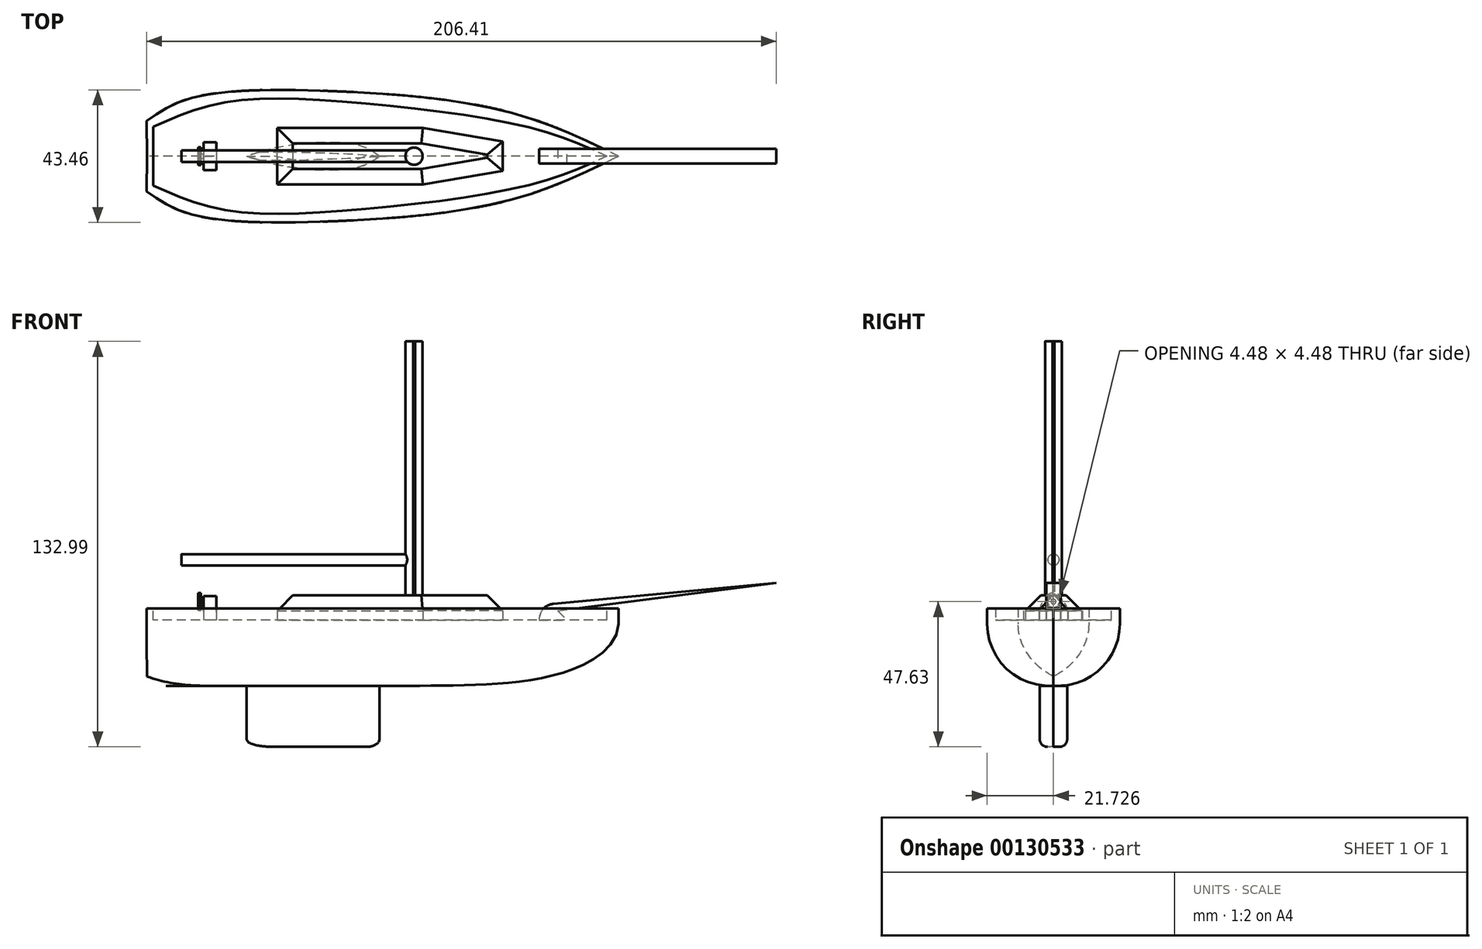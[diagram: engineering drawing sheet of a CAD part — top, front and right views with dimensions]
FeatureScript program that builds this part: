
annotation { "Feature Type Name" : "Feature", "Feature Type Description" : "" }
export const myFeature = defineFeature(function(context is Context, id is Id, definition is map)
    precondition{}
    {
        {
            var Q0;
            Q0=qCreatedBy(makeId("Top.planeOp"),FACE);
            var sketch = newSketch(context, id + "F0", { "sketchPlane" : qUnion([Q0])});
            skLineSegment(sketch, "E0", {"start": v(-76.13, 0) * mm, "end": v(78.37, 0) * mm});
            skFitSpline(sketch, "E1", {"points": [v(78.37, 0) * mm, v(42.4, 14.48) * mm, v(-15.41, 21.34) * mm, v(-61.78, 19.05) * mm, v(-76.34, 11.57) * mm], "startDerivative": vector(-132.35, 64.75) * mm, "endDerivative": vector(-74.5, -52.24) * mm});
            skLineSegment(sketch, "E2", {"start": v(-76.34, 11.57) * mm, "end": v(-76.13, 0) * mm});
            skFitSpline(sketch, "E3.MirrorCS", {"points": [v(78.37, 0) * mm, v(42.4, -14.48) * mm, v(-15.41, -21.34) * mm, v(-61.78, -19.05) * mm, v(-76.34, -11.57) * mm], "startDerivative": vector(-132.35, -64.75) * mm, "endDerivative": vector(-74.5, 52.24) * mm});
            skLineSegment(sketch, "E4.MirrorCS", {"start": v(-76.34, -11.57) * mm, "end": v(-76.13, 0) * mm});
            skSolve(sketch);
        }
        {
            var Q0;
            Q0=makeQuery(id+"F0.imprint","IMPRINT",FACE,{"disambiguationData":[TD([[makeQuery(id+"F0.imprint","IMPRINT",EDGE,{"derivedFrom":sQuery(id+"F0.wireOp",EDGE,"E0")}),1.0]])]});
            var Q1;
            Q1=makeQuery(id+"F0.imprint","IMPRINT",FACE,{"disambiguationData":[TD([[makeQuery(id+"F0.imprint","IMPRINT",EDGE,{"derivedFrom":sQuery(id+"F0.wireOp",EDGE,"E0")}),-1.0]])]});
            extrude(context, id + "F1", {"entities" : qUnion([Q0, Q1]), "depth" : 25.4 * mm});
        }
        {
            var Q0;
            Q0=makeQuery(id+"F1.opExtrude","CAP_EDGE",EDGE,{"disambiguationData":[OSD([sQuery(id+"F0.wireOp",EDGE,"E3.MirrorCS")])],"isStart":true});
            var Q1;
            Q1=makeQuery(id+"F1.opExtrude","CAP_EDGE",EDGE,{"disambiguationData":[OSD([sQuery(id+"F0.wireOp",EDGE,"E1")])],"isStart":true});
            var Q2;
            Q2=makeQuery(id+"F1.opExtrude","CAP_EDGE",EDGE,{"disambiguationData":[OSD([sQuery(id+"F0.wireOp",EDGE,"E4.MirrorCS")])],"isStart":true});
            var Q3;
            Q3=makeQuery(id+"F1.opExtrude","CAP_EDGE",EDGE,{"disambiguationData":[OSD([sQuery(id+"F0.wireOp",EDGE,"E2")])],"isStart":true});
            fillet(context, id + "F2", {"entities" : qUnion([Q0, Q1, Q2, Q3]), "radius" : 20.32 * mm, "tangentPropagation" : true, "allowEdgeOverflow" : false});
        }
        {
            var Q0;
            Q0=makeQuery(id+"F1.opExtrude","CAP_FACE",FACE,{"disambiguationData":[OSD([sQuery(id+"F0.wireOp",EDGE,"E1"),sQuery(id+"F0.wireOp",EDGE,"E2"),sQuery(id+"F0.wireOp",EDGE,"E3.MirrorCS"),sQuery(id+"F0.wireOp",EDGE,"E4.MirrorCS")])],"isStart":false});
            var sketch = newSketch(context, id + "F3", { "sketchPlane" : qUnion([Q0])});
            skLineSegment(sketch, "E5", {"start": v(-76.13, 0) * mm, "end": v(78.37, 0) * mm});
            skFitSpline(sketch, "E6", {"points": [v(74.55, 0) * mm, v(49.26, -9.4) * mm, v(-9.25, -17.68) * mm, v(-51, -17.59) * mm, v(-74.11, -9.66) * mm], "startDerivative": vector(-102.53, -46.86) * mm, "endDerivative": vector(-106.23, 46.73) * mm});
            skLineSegment(sketch, "E7", {"start": v(-74.11, -9.66) * mm, "end": v(-74.11, 0) * mm});
            skLineSegment(sketch, "E8.MirrorCS", {"start": v(-74.11, 9.66) * mm, "end": v(-74.11, 0) * mm});
            skFitSpline(sketch, "E9.MirrorCS", {"points": [v(74.55, 0) * mm, v(49.26, 9.4) * mm, v(-9.25, 17.68) * mm, v(-51, 17.59) * mm, v(-74.11, 9.66) * mm], "startDerivative": vector(-102.53, 46.86) * mm, "endDerivative": vector(-106.23, -46.73) * mm});
            skSolve(sketch);
        }
        {
            var Q0;
            Q0 = qSketchRegion(id + "F3", true);
            extrude(context, id + "F4", {"entities" : qUnion([Q0]), "operationType" : NewBodyOperationType.REMOVE, "oppositeDirection" : true, "depth" : 3.82 * mm});
        }
        {
            var Q0;
            Q0=makeQuery(id+"F4.boolean.opBoolean","COPY",FACE,{"derivedFrom":makeQuery(id+"F4.opExtrude","CAP_FACE",FACE,{"disambiguationData":[OSD([sQuery(id+"F3.wireOp",EDGE,"E6"),sQuery(id+"F3.wireOp",EDGE,"E7"),sQuery(id+"F3.wireOp",EDGE,"E8.MirrorCS"),sQuery(id+"F3.wireOp",EDGE,"E9.MirrorCS")])],"isStart":false})});
            var sketch = newSketch(context, id + "F5", { "sketchPlane" : qUnion([Q0])});
            skLineSegment(sketch, "E10", {"start": v(-74.11, 0) * mm, "end": v(74.55, 0) * mm});
            skLineSegment(sketch, "E11.bottom", {"start": v(-33.52, 9.26) * mm, "end": v(14.21, 9.26) * mm});
            skLineSegment(sketch, "E11.top", {"start": v(-33.52, -9.26) * mm, "end": v(14.21, -9.26) * mm});
            skLineSegment(sketch, "E11.left", {"start": v(-33.52, 9.26) * mm, "end": v(-33.52, -9.26) * mm});
            skLineSegment(sketch, "E11.right", {"start": v(14.21, 9.26) * mm, "end": v(14.21, -9.26) * mm});
            skPoint(sketch, "E11.middle", {"position": v(-9.66, 0) * mm});
            skLineSegment(sketch, "E12", {"start": v(14.21, -9.26) * mm, "end": v(40.42, -4.78) * mm});
            skLineSegment(sketch, "E13", {"start": v(40.42, -4.78) * mm, "end": v(40.42, 0) * mm});
            skLineSegment(sketch, "E14.MirrorCS", {"start": v(14.21, 9.26) * mm, "end": v(40.42, 4.78) * mm});
            skLineSegment(sketch, "E15.MirrorCS", {"start": v(40.42, 4.78) * mm, "end": v(40.42, 0) * mm});
            skLineSegment(sketch, "E16.bottom", {"start": v(-53.41, 4.58) * mm, "end": v(-57.62, 4.58) * mm});
            skLineSegment(sketch, "E16.top", {"start": v(-53.41, -4.58) * mm, "end": v(-57.62, -4.58) * mm});
            skLineSegment(sketch, "E16.left", {"start": v(-53.41, 4.58) * mm, "end": v(-53.41, -4.58) * mm});
            skLineSegment(sketch, "E16.right", {"start": v(-57.62, 4.58) * mm, "end": v(-57.62, -4.58) * mm});
            skPoint(sketch, "E16.middle", {"position": v(-55.52, 0) * mm});
            skSolve(sketch);
        }
        {
            var Q0;
            {var subQ5=sQuery(id+"F5.wireOp",EDGE,"E11.bottom");Q0=makeQuery(id+"F5.imprint","IMPRINT",FACE,{"disambiguationData":[TD([[makeQuery(id+"F5.imprint","IMPRINT",EDGE,{"derivedFrom":subQ5}),-1.0]])]});}
            var Q1;
            {var subQ5=sQuery(id+"F5.wireOp",EDGE,"E11.top");Q1=makeQuery(id+"F5.imprint","IMPRINT",FACE,{"disambiguationData":[TD([[makeQuery(id+"F5.imprint","IMPRINT",EDGE,{"derivedFrom":subQ5}),1.0]])]});}
            var Q2;
            {var subQ4=sQuery(id+"F5.wireOp",EDGE,"E14.MirrorCS");Q2=makeQuery(id+"F5.imprint","IMPRINT",FACE,{"disambiguationData":[TD([[makeQuery(id+"F5.imprint","IMPRINT",EDGE,{"derivedFrom":subQ4}),-1.0]])]});}
            var Q3;
            {var subQ4=sQuery(id+"F5.wireOp",EDGE,"E12");Q3=makeQuery(id+"F5.imprint","IMPRINT",FACE,{"disambiguationData":[TD([[makeQuery(id+"F5.imprint","IMPRINT",EDGE,{"derivedFrom":subQ4}),1.0]])]});}
            extrude(context, id + "F6", {"entities" : qUnion([Q0, Q1, Q2, Q3]), "operationType" : NewBodyOperationType.ADD, "depth" : 8.06 * mm});
        }
        {
            var Q0;
            {var subQ5=sQuery(id+"F5.wireOp",EDGE,"E16.bottom");Q0=makeQuery(id+"F5.imprint","IMPRINT",FACE,{"disambiguationData":[TD([[makeQuery(id+"F5.imprint","IMPRINT",EDGE,{"derivedFrom":subQ5}),1.0]])]});}
            var Q1;
            {var subQ5=sQuery(id+"F5.wireOp",EDGE,"E16.top");Q1=makeQuery(id+"F5.imprint","IMPRINT",FACE,{"disambiguationData":[TD([[makeQuery(id+"F5.imprint","IMPRINT",EDGE,{"derivedFrom":subQ5}),-1.0]])]});}
            extrude(context, id + "F7", {"entities" : qUnion([Q0, Q1]), "operationType" : NewBodyOperationType.ADD, "depth" : 7.85 * mm});
        }
        {
            var Q0;
            Q0=makeQuery(id+"F7.opExtrude","CAP_EDGE",EDGE,{"disambiguationData":[OSD([sQuery(id+"F5.wireOp",EDGE,"E16.bottom")])],"isStart":false});
            var Q1;
            Q1=makeQuery(id+"F7.opExtrude","CAP_EDGE",EDGE,{"disambiguationData":[OSD([sQuery(id+"F5.wireOp",EDGE,"E16.top")])],"isStart":false});
            fillet(context, id + "F8", {"entities" : qUnion([Q0, Q1]), "radius" : 5.08 * mm, "tangentPropagation" : true, "allowEdgeOverflow" : false});
        }
        {
            var Q0;
            Q0=makeQuery(id+"F6.opExtrude","CAP_EDGE",EDGE,{"disambiguationData":[OSD([sQuery(id+"F5.wireOp",EDGE,"E11.bottom")])],"isStart":false});
            var Q1;
            Q1=makeQuery(id+"F6.opExtrude","CAP_EDGE",EDGE,{"disambiguationData":[OSD([sQuery(id+"F5.wireOp",EDGE,"E11.left")])],"isStart":false});
            var Q2;
            Q2=makeQuery(id+"F6.opExtrude","CAP_EDGE",EDGE,{"disambiguationData":[OSD([sQuery(id+"F5.wireOp",EDGE,"E11.top")])],"isStart":false});
            var Q3;
            Q3=makeQuery(id+"F6.opExtrude","CAP_EDGE",EDGE,{"disambiguationData":[OSD([sQuery(id+"F5.wireOp",EDGE,"E12")])],"isStart":false});
            var Q4;
            Q4=makeQuery(id+"F6.opExtrude","CAP_EDGE",EDGE,{"disambiguationData":[OSD([sQuery(id+"F5.wireOp",EDGE,"E14.MirrorCS")])],"isStart":false});
            var Q5;
            Q5=makeQuery(id+"F6.opExtrude","CAP_EDGE",EDGE,{"disambiguationData":[OSD([sQuery(id+"F5.wireOp",EDGE,"E13"),sQuery(id+"F5.wireOp",EDGE,"E15.MirrorCS")])],"isStart":false});
            chamfer(context, id + "F9", {"entities" : qUnion([Q0, Q1, Q2, Q3, Q4, Q5]), "width" : 5.08 * mm, "tangentPropagation" : true});
        }
        {
            var Q0;
            Q0=makeQuery(id+"F7.opExtrude","SWEPT_FACE",FACE,{"disambiguationData":[OSD([sQuery(id+"F5.wireOp",EDGE,"E16.right")])]});
            var sketch = newSketch(context, id + "F10", { "sketchPlane" : qUnion([Q0])});
            skLineSegment(sketch, "E17", {"start": v(0, 29.4) * mm, "end": v(0, 21.58) * mm});
            skCircle(sketch, "E18", {"center": v(0, 27.62) * mm, "radius": 0.8 * mm});
            skSolve(sketch);
        }
        {
            var Q0;
            Q0 = qSketchRegion(id + "F10", true);
            extrude(context, id + "F11", {"entities" : qUnion([Q0]), "operationType" : NewBodyOperationType.ADD, "depth" : 0.96 * mm});
        }
        {
            var Q0;
            Q0=makeQuery(id+"F11.opExtrude","CAP_FACE",FACE,{"disambiguationData":[OSD([sQuery(id+"F10.wireOp",EDGE,"E18")])],"isStart":false});
            var sketch = newSketch(context, id + "F12", { "sketchPlane" : qUnion([Q0])});
            skPoint(sketch, "E19", {"position": v(0, 27.62) * mm});
            skCircle(sketch, "E20", {"center": v(0, 27.62) * mm, "radius": 2.88 * mm});
            skLineSegment(sketch, "E21", {"start": v(0, 27.62) * mm, "end": v(-2.88, 27.62) * mm});
            skLineSegment(sketch, "E22", {"start": v(-2.88, 27.62) * mm, "end": v(2.88, 27.62) * mm});
            skLineSegment(sketch, "E23", {"start": v(2.88, 27.62) * mm, "end": v(0, 27.62) * mm});
            skLineSegment(sketch, "E24", {"start": v(0, 27.62) * mm, "end": v(0, 24.75) * mm});
            skLineSegment(sketch, "E25", {"start": v(0, 24.75) * mm, "end": v(0, 30.5) * mm});
            skLineSegment(sketch, "E26", {"start": v(0, 30.5) * mm, "end": v(-2.88, 30.5) * mm});
            skLineSegment(sketch, "E27", {"start": v(-2.88, 27.62) * mm, "end": v(-2.88, 30.5) * mm});
            skLineSegment(sketch, "E28", {"start": v(0, 30.5) * mm, "end": v(2.88, 30.5) * mm});
            skLineSegment(sketch, "E29", {"start": v(2.88, 27.62) * mm, "end": v(2.88, 30.5) * mm});
            skLineSegment(sketch, "E30", {"start": v(2.88, 27.62) * mm, "end": v(2.88, 24.75) * mm});
            skLineSegment(sketch, "E31", {"start": v(0, 24.75) * mm, "end": v(2.88, 24.75) * mm});
            skLineSegment(sketch, "E32", {"start": v(0, 24.75) * mm, "end": v(-2.88, 24.75) * mm});
            skLineSegment(sketch, "E33", {"start": v(-2.88, 27.62) * mm, "end": v(-2.88, 24.75) * mm});
            skLineSegment(sketch, "E34", {"start": v(0, 27.62) * mm, "end": v(2.88, 30.5) * mm});
            skLineSegment(sketch, "E35", {"start": v(0, 27.62) * mm, "end": v(2.88, 24.75) * mm});
            skLineSegment(sketch, "E36", {"start": v(0, 27.62) * mm, "end": v(-2.88, 24.75) * mm});
            skLineSegment(sketch, "E37", {"start": v(0, 27.62) * mm, "end": v(-2.88, 30.5) * mm});
            skCircle(sketch, "E38", {"center": v(0, 27.62) * mm, "radius": 1.88 * mm});
            skCircle(sketch, "E39", {"center": v(-1.33, 28.96) * mm, "radius": 0.36 * mm});
            skCircle(sketch, "E40", {"center": v(0, 29.5) * mm, "radius": 0.36 * mm});
            skCircle(sketch, "E41", {"center": v(1.33, 28.96) * mm, "radius": 0.35 * mm});
            skCircle(sketch, "E42", {"center": v(1.88, 27.62) * mm, "radius": 0.36 * mm});
            skCircle(sketch, "E43", {"center": v(1.33, 26.3) * mm, "radius": 0.36 * mm});
            skCircle(sketch, "E44", {"center": v(0, 25.74) * mm, "radius": 0.36 * mm});
            skCircle(sketch, "E45", {"center": v(-1.33, 26.3) * mm, "radius": 0.36 * mm});
            skCircle(sketch, "E46", {"center": v(-1.88, 27.62) * mm, "radius": 0.35 * mm});
            skSolve(sketch);
        }
        {
            var Q0;
            {var subQ5=sQuery(id+"F12.wireOp",EDGE,"E34");var subQ6=sQuery(id+"F12.wireOp",EDGE,"E20");var subQ7=makeQuery(id+"F12.imprint","INTERSECT",VERTEX,{"derivedFrom":[subQ6,subQ5]});Q0=makeQuery(id+"F12.imprint","IMPRINT",FACE,{"disambiguationData":[TD([[makeQuery(id+"F12.imprint","IMPRINT",EDGE,{"disambiguationData":[TD([[subQ7,1.0]])],"derivedFrom":subQ5}),-1.0]])]});}
            var Q1;
            {var subQ5=sQuery(id+"F12.wireOp",EDGE,"E34");var subQ6=sQuery(id+"F12.wireOp",EDGE,"E20");var subQ7=makeQuery(id+"F12.imprint","INTERSECT",VERTEX,{"derivedFrom":[subQ6,subQ5]});Q1=makeQuery(id+"F12.imprint","IMPRINT",FACE,{"disambiguationData":[TD([[makeQuery(id+"F12.imprint","IMPRINT",EDGE,{"disambiguationData":[TD([[subQ7,1.0]])],"derivedFrom":subQ5}),1.0]])]});}
            var Q2;
            {var subQ5=sQuery(id+"F12.wireOp",EDGE,"E37");var subQ6=sQuery(id+"F12.wireOp",EDGE,"E20");var subQ7=makeQuery(id+"F12.imprint","INTERSECT",VERTEX,{"derivedFrom":[subQ6,subQ5]});Q2=makeQuery(id+"F12.imprint","IMPRINT",FACE,{"disambiguationData":[TD([[makeQuery(id+"F12.imprint","IMPRINT",EDGE,{"disambiguationData":[TD([[subQ7,1.0]])],"derivedFrom":subQ5}),-1.0]])]});}
            var Q3;
            {var subQ5=sQuery(id+"F12.wireOp",EDGE,"E37");var subQ6=sQuery(id+"F12.wireOp",EDGE,"E20");var subQ7=makeQuery(id+"F12.imprint","INTERSECT",VERTEX,{"derivedFrom":[subQ6,subQ5]});Q3=makeQuery(id+"F12.imprint","IMPRINT",FACE,{"disambiguationData":[TD([[makeQuery(id+"F12.imprint","IMPRINT",EDGE,{"disambiguationData":[TD([[subQ7,1.0]])],"derivedFrom":subQ5}),1.0]])]});}
            var Q4;
            {var subQ5=sQuery(id+"F12.wireOp",EDGE,"E36");var subQ6=sQuery(id+"F12.wireOp",EDGE,"E20");var subQ7=makeQuery(id+"F12.imprint","INTERSECT",VERTEX,{"derivedFrom":[subQ6,subQ5]});Q4=makeQuery(id+"F12.imprint","IMPRINT",FACE,{"disambiguationData":[TD([[makeQuery(id+"F12.imprint","IMPRINT",EDGE,{"disambiguationData":[TD([[subQ7,1.0]])],"derivedFrom":subQ5}),-1.0]])]});}
            var Q5;
            {var subQ7=sQuery(id+"F12.wireOp",EDGE,"E36");var subQ8=sQuery(id+"F12.wireOp",EDGE,"E20");var subQ9=makeQuery(id+"F12.imprint","INTERSECT",VERTEX,{"derivedFrom":[subQ8,subQ7]});Q5=makeQuery(id+"F12.imprint","IMPRINT",FACE,{"disambiguationData":[TD([[makeQuery(id+"F12.imprint","IMPRINT",EDGE,{"disambiguationData":[TD([[subQ9,1.0]])],"derivedFrom":subQ7}),1.0]])]});}
            var Q6;
            {var subQ5=sQuery(id+"F12.wireOp",EDGE,"E35");var subQ6=sQuery(id+"F12.wireOp",EDGE,"E20");var subQ7=makeQuery(id+"F12.imprint","INTERSECT",VERTEX,{"derivedFrom":[subQ6,subQ5]});Q6=makeQuery(id+"F12.imprint","IMPRINT",FACE,{"disambiguationData":[TD([[makeQuery(id+"F12.imprint","IMPRINT",EDGE,{"disambiguationData":[TD([[subQ7,1.0]])],"derivedFrom":subQ5}),-1.0]])]});}
            var Q7;
            {var subQ5=sQuery(id+"F12.wireOp",EDGE,"E35");var subQ6=sQuery(id+"F12.wireOp",EDGE,"E20");var subQ7=makeQuery(id+"F12.imprint","INTERSECT",VERTEX,{"derivedFrom":[subQ6,subQ5]});Q7=makeQuery(id+"F12.imprint","IMPRINT",FACE,{"disambiguationData":[TD([[makeQuery(id+"F12.imprint","IMPRINT",EDGE,{"disambiguationData":[TD([[subQ7,1.0]])],"derivedFrom":subQ5}),1.0]])]});}
            var Q8;
            {var subQ5=sQuery(id+"F12.wireOp",EDGE,"E46");var subQ7=sQuery(id+"F12.wireOp",EDGE,"E22");var subQ11=makeQuery(id+"F12.imprint","INTERSECT",VERTEX,{"disambiguationData":[OD(1.0)],"derivedFrom":[subQ7,subQ5]});Q8=makeQuery(id+"F12.imprint","IMPRINT",FACE,{"disambiguationData":[TD([[makeQuery(id+"F12.imprint","IMPRINT",EDGE,{"disambiguationData":[TD([[subQ11,-1.0]])],"derivedFrom":subQ7}),1.0]])]});}
            var Q9;
            {var subQ0=sQuery(id+"F12.wireOp",EDGE,"E40");var subQ1=sQuery(id+"F12.wireOp",EDGE,"E25");var subQ2=makeQuery(id+"F12.imprint","INTERSECT",VERTEX,{"disambiguationData":[OD(0.0)],"derivedFrom":[subQ1,subQ0]});Q9=makeQuery(id+"F12.imprint","IMPRINT",FACE,{"disambiguationData":[TD([[makeQuery(id+"F12.imprint","IMPRINT",EDGE,{"disambiguationData":[TD([[subQ2,1.0]])],"derivedFrom":subQ1}),-1.0]])]});}
            var Q10;
            {var subQ0=sQuery(id+"F12.wireOp",EDGE,"E42");var subQ1=sQuery(id+"F12.wireOp",EDGE,"E23");var subQ2=makeQuery(id+"F12.imprint","INTERSECT",VERTEX,{"disambiguationData":[OD(1.0)],"derivedFrom":[subQ1,subQ0]});Q10=makeQuery(id+"F12.imprint","IMPRINT",FACE,{"disambiguationData":[TD([[makeQuery(id+"F12.imprint","IMPRINT",EDGE,{"disambiguationData":[TD([[subQ2,-1.0]])],"derivedFrom":subQ1}),1.0]])]});}
            var Q11;
            {var subQ3=sQuery(id+"F12.wireOp",EDGE,"E44");var subQ5=sQuery(id+"F12.wireOp",EDGE,"E25");var subQ6=makeQuery(id+"F12.imprint","INTERSECT",VERTEX,{"disambiguationData":[OD(1.0)],"derivedFrom":[subQ5,subQ3]});Q11=makeQuery(id+"F12.imprint","IMPRINT",FACE,{"disambiguationData":[TD([[makeQuery(id+"F12.imprint","IMPRINT",EDGE,{"disambiguationData":[TD([[subQ6,-1.0]])],"derivedFrom":subQ5}),1.0]])]});}
            var Q12;
            {var subQ1=sQuery(id+"F12.wireOp",EDGE,"E25");var subQ3=makeQuery(id+"F11.opExtrude","CAP_EDGE",EDGE,{"disambiguationData":[OSD([sQuery(id+"F10.wireOp",EDGE,"E18")])],"isStart":false});var subQ4=makeQuery(id+"F12.imprint","INTERSECT",VERTEX,{"disambiguationData":[OD(1.0)],"derivedFrom":[subQ3,subQ1]});Q12=makeQuery(id+"F12.imprint","IMPRINT",FACE,{"disambiguationData":[TD([[makeQuery(id+"F12.imprint","IMPRINT",EDGE,{"disambiguationData":[TD([[subQ4,1.0]])],"derivedFrom":subQ3}),1.0]])]});}
            var Q13;
            {var subQ1=sQuery(id+"F12.wireOp",EDGE,"E22");var subQ3=makeQuery(id+"F11.opExtrude","CAP_EDGE",EDGE,{"disambiguationData":[OSD([sQuery(id+"F10.wireOp",EDGE,"E18")])],"isStart":false});var subQ4=makeQuery(id+"F12.imprint","INTERSECT",VERTEX,{"derivedFrom":[subQ3,subQ1]});Q13=makeQuery(id+"F12.imprint","IMPRINT",FACE,{"disambiguationData":[TD([[makeQuery(id+"F12.imprint","IMPRINT",EDGE,{"disambiguationData":[TD([[subQ4,1.0]])],"derivedFrom":subQ3}),1.0]])]});}
            var Q14;
            {var subQ1=sQuery(id+"F12.wireOp",EDGE,"E22");var subQ3=makeQuery(id+"F11.opExtrude","CAP_EDGE",EDGE,{"disambiguationData":[OSD([sQuery(id+"F10.wireOp",EDGE,"E18")])],"isStart":false});var subQ4=makeQuery(id+"F12.imprint","INTERSECT",VERTEX,{"derivedFrom":[subQ3,subQ1]});Q14=makeQuery(id+"F12.imprint","IMPRINT",FACE,{"disambiguationData":[TD([[makeQuery(id+"F12.imprint","IMPRINT",EDGE,{"disambiguationData":[TD([[subQ4,-1.0]])],"derivedFrom":subQ3}),1.0]])]});}
            var Q15;
            {var subQ1=sQuery(id+"F12.wireOp",EDGE,"E25");var subQ3=makeQuery(id+"F11.opExtrude","CAP_EDGE",EDGE,{"disambiguationData":[OSD([sQuery(id+"F10.wireOp",EDGE,"E18")])],"isStart":false});var subQ4=makeQuery(id+"F12.imprint","INTERSECT",VERTEX,{"disambiguationData":[OD(0.0)],"derivedFrom":[subQ3,subQ1]});Q15=makeQuery(id+"F12.imprint","IMPRINT",FACE,{"disambiguationData":[TD([[makeQuery(id+"F12.imprint","IMPRINT",EDGE,{"disambiguationData":[TD([[subQ4,1.0]])],"derivedFrom":subQ3}),1.0]])]});}
            var Q16;
            {var subQ1=sQuery(id+"F12.wireOp",EDGE,"E25");var subQ3=makeQuery(id+"F11.opExtrude","CAP_EDGE",EDGE,{"disambiguationData":[OSD([sQuery(id+"F10.wireOp",EDGE,"E18")])],"isStart":false});var subQ4=makeQuery(id+"F12.imprint","INTERSECT",VERTEX,{"disambiguationData":[OD(0.0)],"derivedFrom":[subQ3,subQ1]});Q16=makeQuery(id+"F12.imprint","IMPRINT",FACE,{"disambiguationData":[TD([[makeQuery(id+"F12.imprint","IMPRINT",EDGE,{"disambiguationData":[TD([[subQ4,-1.0]])],"derivedFrom":subQ3}),1.0]])]});}
            var Q17;
            {var subQ1=sQuery(id+"F12.wireOp",EDGE,"E23");var subQ3=makeQuery(id+"F11.opExtrude","CAP_EDGE",EDGE,{"disambiguationData":[OSD([sQuery(id+"F10.wireOp",EDGE,"E18")])],"isStart":false});var subQ4=makeQuery(id+"F12.imprint","INTERSECT",VERTEX,{"derivedFrom":[subQ3,subQ1]});Q17=makeQuery(id+"F12.imprint","IMPRINT",FACE,{"disambiguationData":[TD([[makeQuery(id+"F12.imprint","IMPRINT",EDGE,{"disambiguationData":[TD([[subQ4,1.0]])],"derivedFrom":subQ3}),1.0]])]});}
            var Q18;
            {var subQ1=sQuery(id+"F12.wireOp",EDGE,"E23");var subQ3=makeQuery(id+"F11.opExtrude","CAP_EDGE",EDGE,{"disambiguationData":[OSD([sQuery(id+"F10.wireOp",EDGE,"E18")])],"isStart":false});var subQ4=makeQuery(id+"F12.imprint","INTERSECT",VERTEX,{"derivedFrom":[subQ3,subQ1]});Q18=makeQuery(id+"F12.imprint","IMPRINT",FACE,{"disambiguationData":[TD([[makeQuery(id+"F12.imprint","IMPRINT",EDGE,{"disambiguationData":[TD([[subQ4,-1.0]])],"derivedFrom":subQ3}),1.0]])]});}
            var Q19;
            {var subQ1=sQuery(id+"F12.wireOp",EDGE,"E25");var subQ3=makeQuery(id+"F11.opExtrude","CAP_EDGE",EDGE,{"disambiguationData":[OSD([sQuery(id+"F10.wireOp",EDGE,"E18")])],"isStart":false});var subQ4=makeQuery(id+"F12.imprint","INTERSECT",VERTEX,{"disambiguationData":[OD(1.0)],"derivedFrom":[subQ3,subQ1]});Q19=makeQuery(id+"F12.imprint","IMPRINT",FACE,{"disambiguationData":[TD([[makeQuery(id+"F12.imprint","IMPRINT",EDGE,{"disambiguationData":[TD([[subQ4,-1.0]])],"derivedFrom":subQ3}),1.0]])]});}
            extrude(context, id + "F13", {"entities" : qUnion([Q0, Q1, Q2, Q3, Q4, Q5, Q6, Q7, Q8, Q9, Q10, Q11, Q12, Q13, Q14, Q15, Q16, Q17, Q18, Q19]), "operationType" : NewBodyOperationType.ADD, "depth" : 0.83 * mm});
        }
        {
            var Q0;
            Q0=makeQuery(id+"F4.boolean.opBoolean","COPY",FACE,{"derivedFrom":makeQuery(id+"F4.opExtrude","CAP_FACE",FACE,{"disambiguationData":[OSD([sQuery(id+"F3.wireOp",EDGE,"E6"),sQuery(id+"F3.wireOp",EDGE,"E7"),sQuery(id+"F3.wireOp",EDGE,"E8.MirrorCS"),sQuery(id+"F3.wireOp",EDGE,"E9.MirrorCS")])],"isStart":false})});
            var sketch = newSketch(context, id + "F14", { "sketchPlane" : qUnion([Q0])});
            skLineSegment(sketch, "E47", {"start": v(40.42, 0) * mm, "end": v(74.55, 0) * mm});
            skLineSegment(sketch, "E48.bottom", {"start": v(52.36, 2.39) * mm, "end": v(63.86, 2.39) * mm});
            skLineSegment(sketch, "E48.top", {"start": v(52.36, -2.39) * mm, "end": v(63.86, -2.39) * mm});
            skLineSegment(sketch, "E48.left", {"start": v(52.36, 2.39) * mm, "end": v(52.36, -2.39) * mm});
            skLineSegment(sketch, "E48.right", {"start": v(63.86, 2.39) * mm, "end": v(63.86, -2.39) * mm});
            skPoint(sketch, "E48.middle", {"position": v(58.11, 0) * mm});
            skSolve(sketch);
        }
        {
            var Q0;
            Q0 = qSketchRegion(id + "F14", true);
            extrude(context, id + "F15", {"entities" : qUnion([Q0]), "operationType" : NewBodyOperationType.ADD, "depth" : 5.24 * mm});
        }
        {
            var Q0;
            Q0=makeQuery(id+"F15.opExtrude","CAP_EDGE",EDGE,{"disambiguationData":[OSD([sQuery(id+"F14.wireOp",EDGE,"E48.right")])],"isStart":false});
            chamfer(context, id + "F16", {"entities" : qUnion([Q0]), "width" : 7.62 * mm, "tangentPropagation" : true});
        }
        {
            var Q0;
            Q0=makeQuery(id+"F15.opExtrude","SWEPT_FACE",FACE,{"disambiguationData":[OSD([sQuery(id+"F14.wireOp",EDGE,"E48.top")])]});
            var sketch = newSketch(context, id + "F17", { "sketchPlane" : qUnion([Q0])});
            skLineSegment(sketch, "E49", {"start": v(58.44, 24.61) * mm, "end": v(130.07, 33.81) * mm});
            skLineSegment(sketch, "E50", {"start": v(130.07, 33.81) * mm, "end": v(56.24, 26.82) * mm});
            skSolve(sketch);
        }
        {
            var Q0;
            Q0 = qSketchRegion(id + "F17", true);
            var Q1;
            {var subQ0=sQuery(id+"F17.wireOp",EDGE,"E49");Q1=makeQuery(id+"F17.imprint","IMPRINT",FACE,{"disambiguationData":[TD([[makeQuery(id+"F17.imprint","IMPRINT",EDGE,{"derivedFrom":subQ0}),1.0]])]});}
            extrude(context, id + "F18", {"entities" : qUnion([Q0, Q1]), "operationType" : NewBodyOperationType.ADD, "oppositeDirection" : true, "depth" : 4.78 * mm});
        }
        {
            var Q0;
            Q0=makeQuery(id+"F15.opExtrude","CAP_EDGE",EDGE,{"disambiguationData":[OSD([sQuery(id+"F14.wireOp",EDGE,"E48.left")])],"isStart":false});
            fillet(context, id + "F19", {"entities" : qUnion([Q0]), "radius" : 5.08 * mm, "tangentPropagation" : true, "allowEdgeOverflow" : false});
        }
        {
            var Q0;
            Q0=makeQuery(id+"F6.opExtrude","CAP_FACE",FACE,{"disambiguationData":[OSD([sQuery(id+"F5.wireOp",EDGE,"E11.bottom"),sQuery(id+"F5.wireOp",EDGE,"E11.top"),sQuery(id+"F5.wireOp",EDGE,"E11.left"),sQuery(id+"F5.wireOp",EDGE,"E12"),sQuery(id+"F5.wireOp",EDGE,"E13"),sQuery(id+"F5.wireOp",EDGE,"E14.MirrorCS"),sQuery(id+"F5.wireOp",EDGE,"E15.MirrorCS")])],"isStart":false});
            var sketch = newSketch(context, id + "F20", { "sketchPlane" : qUnion([Q0])});
            skLineSegment(sketch, "E51", {"start": v(-28.44, 0) * mm, "end": v(35.34, 0) * mm});
            skCircle(sketch, "E52", {"center": v(11.33, 0) * mm, "radius": 2.78 * mm});
            skLineSegment(sketch, "E53.bottom", {"start": v(14.08, -2.76) * mm, "end": v(8.58, -2.76) * mm});
            skLineSegment(sketch, "E53.top", {"start": v(14.08, 2.76) * mm, "end": v(8.58, 2.76) * mm});
            skLineSegment(sketch, "E53.left", {"start": v(14.08, -2.76) * mm, "end": v(14.08, 2.76) * mm});
            skLineSegment(sketch, "E53.right", {"start": v(8.58, -2.76) * mm, "end": v(8.58, 2.76) * mm});
            skSolve(sketch);
        }
        {
            var Q0;
            Q0 = qSketchRegion(id + "F20", true);
            extrude(context, id + "F21", {"entities" : qUnion([Q0]), "operationType" : NewBodyOperationType.ADD, "depth" : 83.34 * mm});
        }
        {
            var Q0;
            Q0=qCreatedBy(makeId("Right.planeOp"),FACE);
            var sketch = newSketch(context, id + "F22", { "sketchPlane" : qUnion([Q0])});
            skLineSegment(sketch, "E54", {"start": v(0, 42.94) * mm, "end": v(0, 39.8) * mm});
            skCircle(sketch, "E55", {"center": v(0, 41.37) * mm, "radius": 1.85 * mm});
            skSolve(sketch);
        }
        {
            var Q0;
            Q0 = qSketchRegion(id + "F22", true);
            extrude(context, id + "F23", {"entities" : qUnion([Q0]), "operationType" : NewBodyOperationType.ADD, "depth" : 10.97 * mm});
        }
        {
            var Q0;
            Q0 = qSketchRegion(id + "F22", true);
            extrude(context, id + "F24", {"entities" : qUnion([Q0]), "operationType" : NewBodyOperationType.ADD, "oppositeDirection" : true, "depth" : 64.84 * mm});
        }
        {
            var Q0;
            Q0=makeQuery(id+"F21.opExtrude","SWEPT_EDGE",EDGE,{"disambiguationData":[OSD([sQuery(id+"F20.wireOp",EDGE,"E53.bottom"),sQuery(id+"F20.wireOp",EDGE,"E53.right")])]});
            var Q1;
            Q1=makeQuery(id+"F21.opExtrude","SWEPT_EDGE",EDGE,{"disambiguationData":[OSD([sQuery(id+"F20.wireOp",EDGE,"E53.bottom"),sQuery(id+"F20.wireOp",EDGE,"E53.left")])]});
            var Q2;
            Q2=makeQuery(id+"F21.opExtrude","SWEPT_EDGE",EDGE,{"disambiguationData":[OSD([sQuery(id+"F20.wireOp",EDGE,"E53.top"),sQuery(id+"F20.wireOp",EDGE,"E53.left")])]});
            var Q3;
            Q3=makeQuery(id+"F21.opExtrude","SWEPT_EDGE",EDGE,{"disambiguationData":[OSD([sQuery(id+"F20.wireOp",EDGE,"E53.top"),sQuery(id+"F20.wireOp",EDGE,"E53.right")])]});
            fillet(context, id + "F25", {"entities" : qUnion([Q0, Q1, Q2, Q3]), "radius" : 2.44 * mm, "tangentPropagation" : true, "allowEdgeOverflow" : false});
        }
        {
            var Q0;
            Q0=makeQuery(id+"F1.opExtrude","CAP_FACE",FACE,{"disambiguationData":[OSD([sQuery(id+"F0.wireOp",EDGE,"E1"),sQuery(id+"F0.wireOp",EDGE,"E2"),sQuery(id+"F0.wireOp",EDGE,"E3.MirrorCS"),sQuery(id+"F0.wireOp",EDGE,"E4.MirrorCS")])],"isStart":true});
            var sketch = newSketch(context, id + "F26", { "sketchPlane" : qUnion([Q0])});
            skLineSegment(sketch, "E56", {"start": v(2.35, 0) * mm, "end": v(-54.06, 0) * mm});
            skFitSpline(sketch, "E57", {"points": [v(0, 0) * mm, v(-3.18, 2.14) * mm, v(-9.9, 4.13) * mm, v(-24.9, 4.11) * mm, v(-35.72, 2.32) * mm, v(-43.59, 0) * mm], "startDerivative": vector(-21.87, 16.71) * mm, "endDerivative": vector(-39.22, -12.51) * mm});
            skFitSpline(sketch, "E58.MirrorCS", {"points": [v(0, 0) * mm, v(-3.18, -2.14) * mm, v(-9.9, -4.13) * mm, v(-24.9, -4.11) * mm, v(-35.72, -2.32) * mm, v(-43.59, 0) * mm], "startDerivative": vector(-21.87, -16.71) * mm, "endDerivative": vector(-39.22, 12.51) * mm});
            skSolve(sketch);
        }
        {
            var Q0;
            Q0 = qSketchRegion(id + "F26", true);
            extrude(context, id + "F27", {"entities" : qUnion([Q0]), "operationType" : NewBodyOperationType.ADD, "depth" : 20 * mm});
        }
        {
            var Q0;
            Q0=makeQuery(id+"F27.opExtrude","CAP_EDGE",EDGE,{"disambiguationData":[OSD([sQuery(id+"F26.wireOp",EDGE,"E57")])],"isStart":false});
            var Q1;
            Q1=makeQuery(id+"F27.opExtrude","CAP_EDGE",EDGE,{"disambiguationData":[OSD([sQuery(id+"F26.wireOp",EDGE,"E58.MirrorCS")])],"isStart":false});
            fillet(context, id + "F28", {"entities" : qUnion([Q0, Q1]), "radius" : 2.54 * mm, "tangentPropagation" : true, "allowEdgeOverflow" : false});
        }
    });
